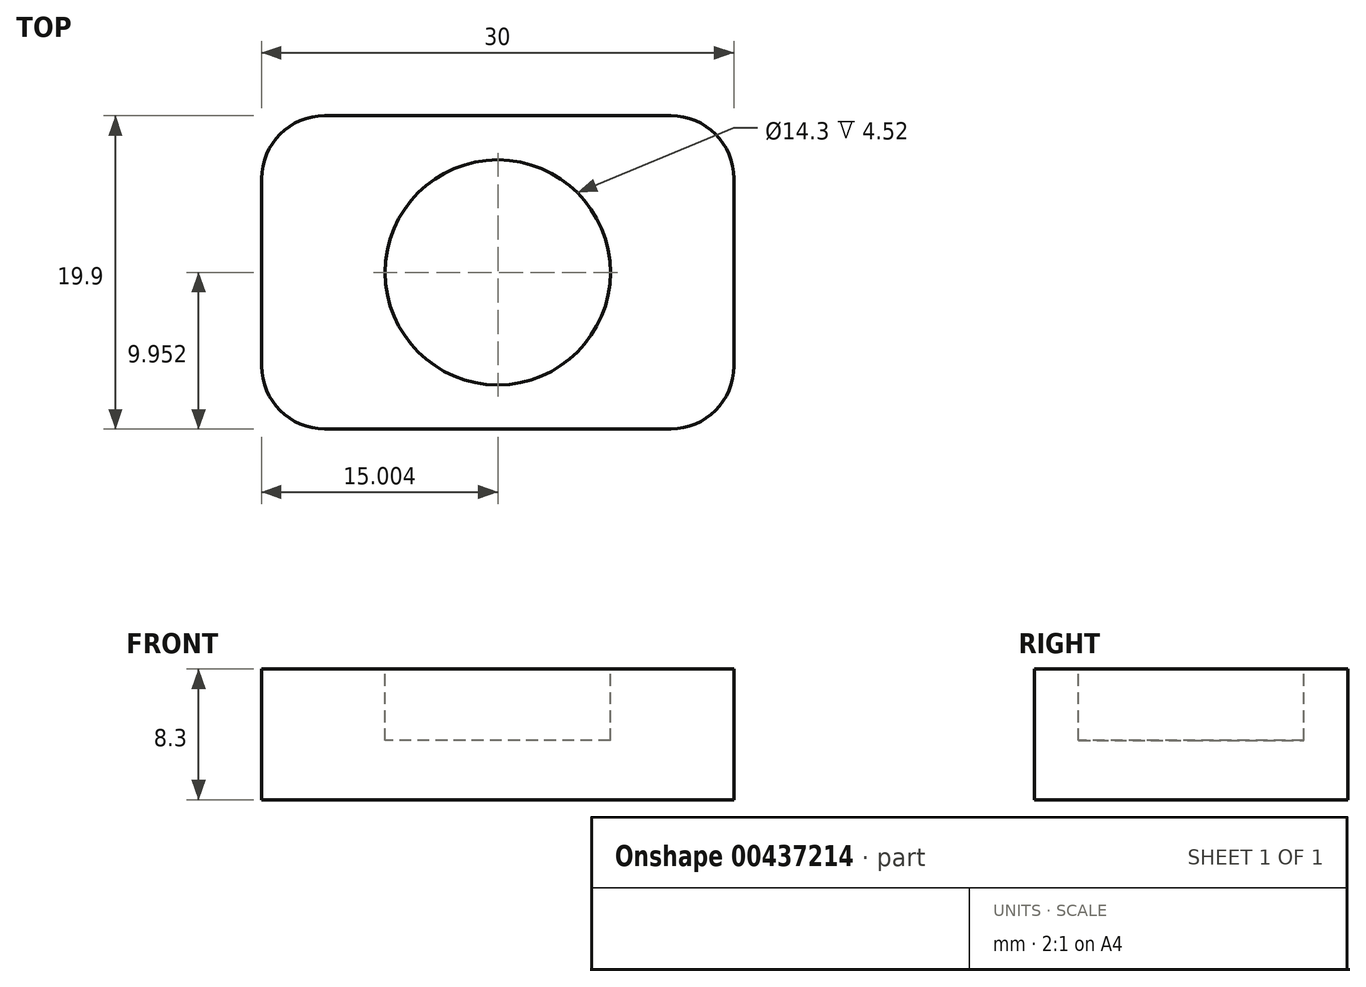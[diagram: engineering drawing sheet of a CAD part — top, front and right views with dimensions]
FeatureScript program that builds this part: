
annotation { "Feature Type Name" : "Feature", "Feature Type Description" : "" }
export const myFeature = defineFeature(function(context is Context, id is Id, definition is map)
    precondition{}
    {
        {
            var Q0;
            Q0=qCreatedBy(makeId("Top.planeOp"),FACE);
            var sketch = newSketch(context, id + "F0", { "sketchPlane" : qUnion([Q0])});
            skLineSegment(sketch, "E0.bottom", {"start": v(-16.02, 5.3) * mm, "end": v(13.98, 5.3) * mm});
            skLineSegment(sketch, "E0.top", {"start": v(-16.02, -14.6) * mm, "end": v(13.98, -14.6) * mm});
            skLineSegment(sketch, "E0.left", {"start": v(-16.02, 5.3) * mm, "end": v(-16.02, -14.6) * mm});
            skLineSegment(sketch, "E0.right", {"start": v(13.98, 5.3) * mm, "end": v(13.98, -14.6) * mm});
            skSolve(sketch);
        }
        {
            var Q0;
            Q0=makeQuery(id+"F0.imprint","IMPRINT",FACE,{"disambiguationData":[TD([[makeQuery(id+"F0.imprint","IMPRINT",EDGE,{"derivedFrom":sQuery(id+"F0.wireOp",EDGE,"E0.bottom")}),-1.0]])]});
            extrude(context, id + "F1", {"entities" : qUnion([Q0]), "depth" : 8.3 * mm});
        }
        {
            var Q0;
            Q0=makeQuery(id+"F1.opExtrude","CAP_FACE",FACE,{"disambiguationData":[OSD([sQuery(id+"F0.wireOp",EDGE,"E0.bottom"),sQuery(id+"F0.wireOp",EDGE,"E0.top"),sQuery(id+"F0.wireOp",EDGE,"E0.left"),sQuery(id+"F0.wireOp",EDGE,"E0.right")])],"isStart":false});
            var sketch = newSketch(context, id + "F2", { "sketchPlane" : qUnion([Q0])});
            skPoint(sketch, "E1", {"position": v(-1.02, -14.6) * mm});
            skPoint(sketch, "E2", {"position": v(-1.02, 5.3) * mm});
            skLineSegment(sketch, "E3", {"start": v(-1.02, 5.3) * mm, "end": v(-1.02, -14.6) * mm, "construction": true});
            skPoint(sketch, "E4", {"position": v(-1.02, -4.66) * mm});
            skCircle(sketch, "E5", {"center": v(-1.02, -4.66) * mm, "radius": 7.15 * mm});
            skSolve(sketch);
        }
        {
            var Q0;
            Q0=makeQuery(id+"F2.imprint","IMPRINT",FACE,{"disambiguationData":[TD([[makeQuery(id+"F2.imprint","IMPRINT",EDGE,{"derivedFrom":sQuery(id+"F2.wireOp",EDGE,"E5")}),1.0]])]});
            var Q1;
            Q1=sQuery(id+"F2.wireOp",EDGE,"E5");
            extrude(context, id + "F3", {"entities" : qUnion([Q0]), "operationType" : NewBodyOperationType.REMOVE, "surfaceEntities" : qUnion([Q1]), "oppositeDirection" : true, "depth" : 4.52 * mm});
        }
        {
            var Q0;
            Q0=makeQuery(id+"F1.opExtrude","SWEPT_EDGE",EDGE,{"disambiguationData":[OSD([sQuery(id+"F0.wireOp",EDGE,"E0.top"),sQuery(id+"F0.wireOp",EDGE,"E0.right")])]});
            var Q1;
            Q1=makeQuery(id+"F1.opExtrude","SWEPT_EDGE",EDGE,{"disambiguationData":[OSD([sQuery(id+"F0.wireOp",EDGE,"E0.top"),sQuery(id+"F0.wireOp",EDGE,"E0.left")])]});
            var Q2;
            Q2=makeQuery(id+"F1.opExtrude","SWEPT_EDGE",EDGE,{"disambiguationData":[OSD([sQuery(id+"F0.wireOp",EDGE,"E0.bottom"),sQuery(id+"F0.wireOp",EDGE,"E0.right")])]});
            var Q3;
            Q3=makeQuery(id+"F1.opExtrude","SWEPT_EDGE",EDGE,{"disambiguationData":[OSD([sQuery(id+"F0.wireOp",EDGE,"E0.bottom"),sQuery(id+"F0.wireOp",EDGE,"E0.left")])]});
            fillet(context, id + "F4", {"entities" : qUnion([Q0, Q1, Q2, Q3]), "radius" : 4 * mm, "tangentPropagation" : true, "allowEdgeOverflow" : false});
        }
    });
